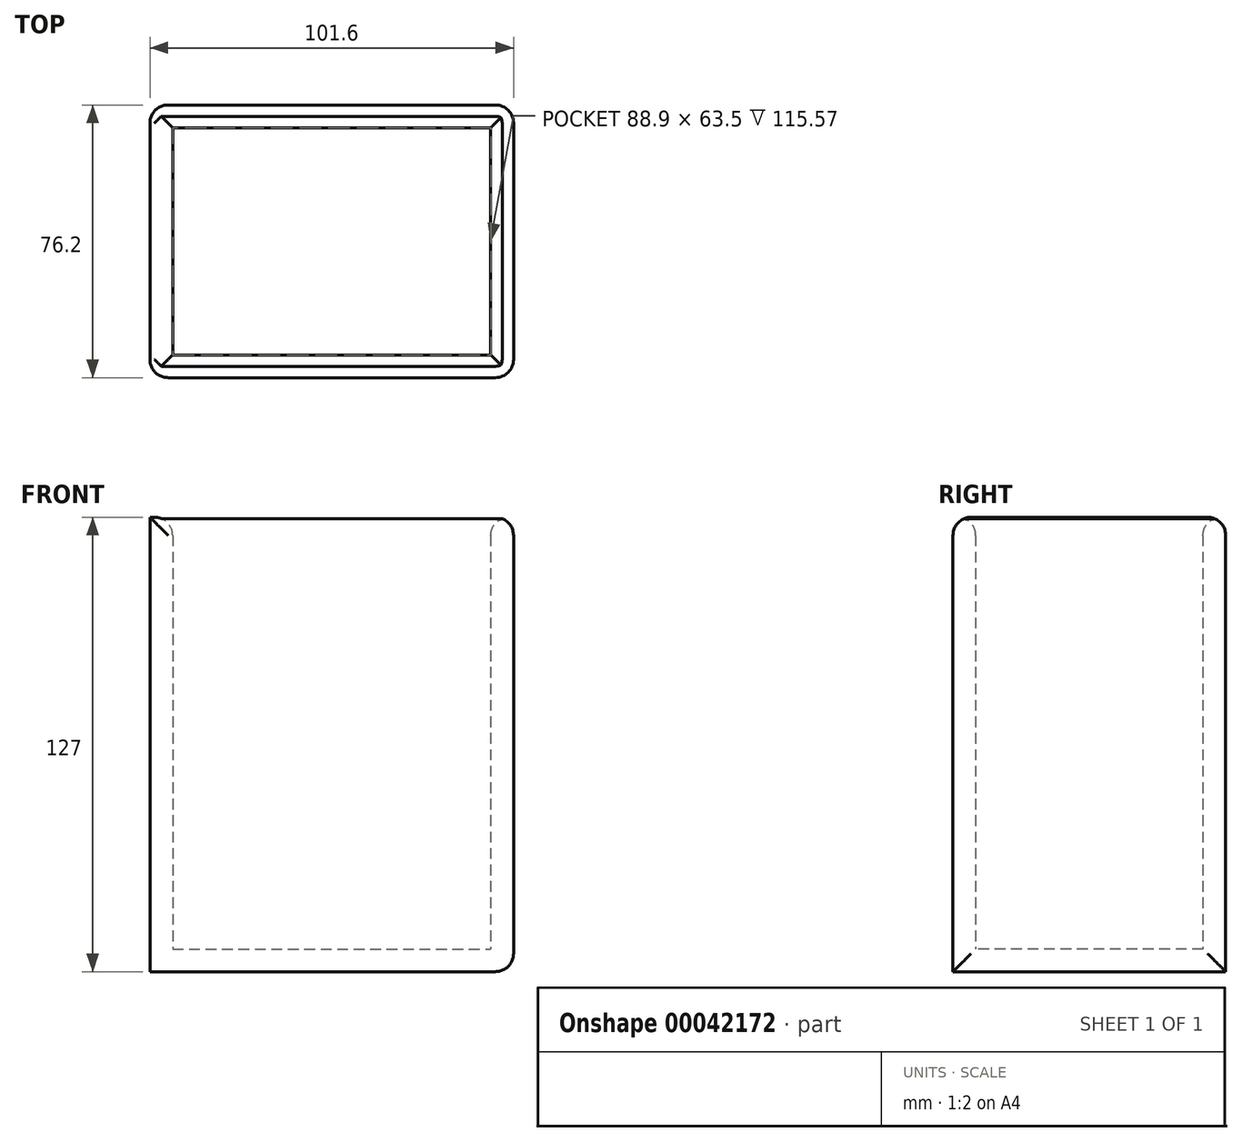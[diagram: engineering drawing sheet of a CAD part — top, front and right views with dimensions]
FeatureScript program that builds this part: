
annotation { "Feature Type Name" : "Feature", "Feature Type Description" : "" }
export const myFeature = defineFeature(function(context is Context, id is Id, definition is map)
    precondition{}
    {
        {
            var Q0;
            Q0=qCreatedBy(makeId("Top.planeOp"),FACE);
            var sketch = newSketch(context, id + "F0", { "sketchPlane" : qUnion([Q0])});
            skLineSegment(sketch, "E0.bottom", {"start": v(23.95, 24.88) * mm, "end": v(125.55, 24.88) * mm});
            skLineSegment(sketch, "E0.top", {"start": v(23.95, -51.32) * mm, "end": v(125.55, -51.32) * mm});
            skLineSegment(sketch, "E0.left", {"start": v(23.95, 24.88) * mm, "end": v(23.95, -51.32) * mm});
            skLineSegment(sketch, "E0.right", {"start": v(125.55, 24.88) * mm, "end": v(125.55, -51.32) * mm});
            skSolve(sketch);
        }
        {
            var Q0;
            Q0=makeQuery(id+"F0.imprint","IMPRINT",FACE,{"disambiguationData":[TD([[makeQuery(id+"F0.imprint","IMPRINT",EDGE,{"derivedFrom":sQuery(id+"F0.wireOp",EDGE,"E0.bottom")}),-1.0]])]});
            extrude(context, id + "F1", {"entities" : qUnion([Q0]), "depth" : 127 * mm});
        }
        {
            var Q0;
            Q0=makeQuery(id+"F1.opExtrude","CAP_FACE",FACE,{"disambiguationData":[OSD([sQuery(id+"F0.wireOp",EDGE,"E0.bottom"),sQuery(id+"F0.wireOp",EDGE,"E0.top"),sQuery(id+"F0.wireOp",EDGE,"E0.left"),sQuery(id+"F0.wireOp",EDGE,"E0.right")])],"isStart":false});
            shell(context, id + "F2", {"entities" : qUnion([Q0]), "thickness" : 6.35 * mm});
        }
        {
            var Q0;
            Q0=makeQuery(id+"F1.opExtrude","SWEPT_EDGE",EDGE,{"disambiguationData":[OSD([sQuery(id+"F0.wireOp",EDGE,"E0.bottom"),sQuery(id+"F0.wireOp",EDGE,"E0.left")])]});
            var Q1;
            Q1=makeQuery(id+"F1.opExtrude","SWEPT_EDGE",EDGE,{"disambiguationData":[OSD([sQuery(id+"F0.wireOp",EDGE,"E0.bottom"),sQuery(id+"F0.wireOp",EDGE,"E0.right")])]});
            var Q2;
            Q2=makeQuery(id+"F1.opExtrude","SWEPT_EDGE",EDGE,{"disambiguationData":[OSD([sQuery(id+"F0.wireOp",EDGE,"E0.top"),sQuery(id+"F0.wireOp",EDGE,"E0.left")])]});
            var Q3;
            Q3=makeQuery(id+"F1.opExtrude","SWEPT_FACE",FACE,{"disambiguationData":[OSD([sQuery(id+"F0.wireOp",EDGE,"E0.right")])]});
            var Q4;
            Q4=makeQuery(id+"F1.opExtrude","CAP_EDGE",EDGE,{"disambiguationData":[OSD([sQuery(id+"F0.wireOp",EDGE,"E0.top")])],"isStart":false});
            var Q5;
            {var subQ0=sQuery(id+"F0.wireOp",EDGE,"E0.bottom");Q5=makeQuery(id+"F2.opShell","OFFSET_EDGE",EDGE,{"disambiguationData":[OSD([subQ0]),TDD([makeQuery(id+"F1.opExtrude","CAP_EDGE",EDGE,{"disambiguationData":[OSD([subQ0])],"isStart":false})])]});}
            var Q6;
            Q6=makeQuery(id+"F1.opExtrude","CAP_EDGE",EDGE,{"disambiguationData":[OSD([sQuery(id+"F0.wireOp",EDGE,"E0.bottom")])],"isStart":false});
            var Q7;
            {var subQ0=sQuery(id+"F0.wireOp",EDGE,"E0.left");Q7=makeQuery(id+"F2.opShell","OFFSET_EDGE",EDGE,{"disambiguationData":[OSD([subQ0]),TDD([makeQuery(id+"F1.opExtrude","CAP_EDGE",EDGE,{"disambiguationData":[OSD([subQ0])],"isStart":false})])]});}
            var Q8;
            {var subQ0=sQuery(id+"F0.wireOp",EDGE,"E0.top");Q8=makeQuery(id+"F2.opShell","OFFSET_EDGE",EDGE,{"disambiguationData":[OSD([subQ0]),TDD([makeQuery(id+"F1.opExtrude","CAP_EDGE",EDGE,{"disambiguationData":[OSD([subQ0])],"isStart":false})])]});}
            var Q9;
            {var subQ0=sQuery(id+"F0.wireOp",EDGE,"E0.right");Q9=makeQuery(id+"F2.opShell","OFFSET_EDGE",EDGE,{"disambiguationData":[OSD([subQ0]),TDD([makeQuery(id+"F1.opExtrude","CAP_EDGE",EDGE,{"disambiguationData":[OSD([subQ0])],"isStart":false})])]});}
            fillet(context, id + "F3", {"entities" : qUnion([Q0, Q1, Q2, Q3, Q4, Q5, Q6, Q7, Q8, Q9]), "radius" : 5.08 * mm, "tangentPropagation" : true, "allowEdgeOverflow" : false});
        }
    });
